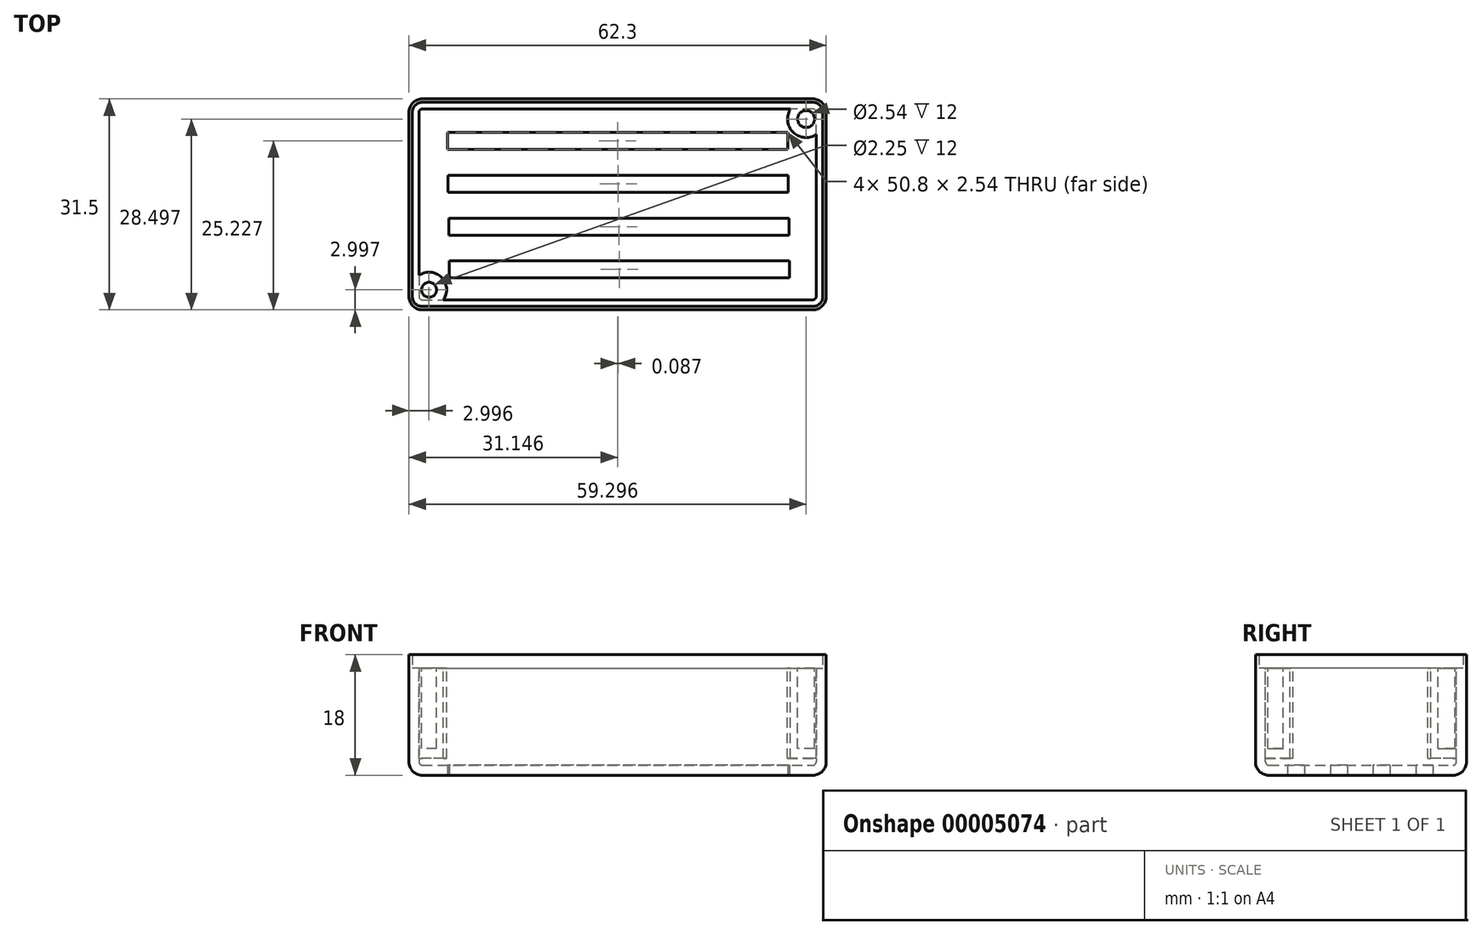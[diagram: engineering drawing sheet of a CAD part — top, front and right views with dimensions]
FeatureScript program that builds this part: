
annotation { "Feature Type Name" : "Feature", "Feature Type Description" : "" }
export const myFeature = defineFeature(function(context is Context, id is Id, definition is map)
    precondition{}
    {
        {
            var Q0;
            Q0=qCreatedBy(makeId("Top.planeOp"),FACE);
            var sketch = newSketch(context, id + "F0", { "sketchPlane" : qUnion([Q0])});
            skLineSegment(sketch, "E0.bottom", {"start": v(-32.94, 23.2) * mm, "end": v(29.36, 23.2) * mm});
            skLineSegment(sketch, "E0.top", {"start": v(-32.94, -8.3) * mm, "end": v(29.36, -8.3) * mm});
            skLineSegment(sketch, "E0.left", {"start": v(-32.94, 23.2) * mm, "end": v(-32.94, -8.3) * mm});
            skLineSegment(sketch, "E0.right", {"start": v(29.36, 23.2) * mm, "end": v(29.36, -8.3) * mm});
            skSolve(sketch);
        }
        {
            var Q0;
            Q0=makeQuery(id+"F0.imprint","IMPRINT",FACE,{"disambiguationData":[TD([[makeQuery(id+"F0.imprint","IMPRINT",EDGE,{"derivedFrom":sQuery(id+"F0.wireOp",EDGE,"E0.bottom")}),-1.0]])]});
            extrude(context, id + "F1", {"entities" : qUnion([Q0]), "depth" : 16 * mm});
        }
        {
            var Q0;
            Q0=makeQuery(id+"F1.opExtrude","CAP_FACE",FACE,{"disambiguationData":[OSD([sQuery(id+"F0.wireOp",EDGE,"E0.bottom"),sQuery(id+"F0.wireOp",EDGE,"E0.top"),sQuery(id+"F0.wireOp",EDGE,"E0.left"),sQuery(id+"F0.wireOp",EDGE,"E0.right")])],"isStart":false});
            var sketch = newSketch(context, id + "F2", { "sketchPlane" : qUnion([Q0])});
            skCircle(sketch, "E1", {"center": v(-29.94, -5.3) * mm, "radius": 1.13 * mm});
            skCircle(sketch, "E2", {"center": v(26.36, 20.2) * mm, "radius": 1.27 * mm});
            skSolve(sketch);
        }
        {
            var Q0;
            Q0=makeQuery(id+"F1.opExtrude","SWEPT_EDGE",EDGE,{"disambiguationData":[OSD([sQuery(id+"F0.wireOp",EDGE,"E0.top"),sQuery(id+"F0.wireOp",EDGE,"E0.left")])]});
            var Q1;
            Q1=makeQuery(id+"F1.opExtrude","SWEPT_EDGE",EDGE,{"disambiguationData":[OSD([sQuery(id+"F0.wireOp",EDGE,"E0.top"),sQuery(id+"F0.wireOp",EDGE,"E0.right")])]});
            var Q2;
            Q2=makeQuery(id+"F1.opExtrude","SWEPT_EDGE",EDGE,{"disambiguationData":[OSD([sQuery(id+"F0.wireOp",EDGE,"E0.bottom"),sQuery(id+"F0.wireOp",EDGE,"E0.right")])]});
            var Q3;
            Q3=makeQuery(id+"F1.opExtrude","SWEPT_EDGE",EDGE,{"disambiguationData":[OSD([sQuery(id+"F0.wireOp",EDGE,"E0.bottom"),sQuery(id+"F0.wireOp",EDGE,"E0.left")])]});
            var Q4;
            Q4=makeQuery(id+"F1.opExtrude","CAP_FACE",FACE,{"disambiguationData":[OSD([sQuery(id+"F0.wireOp",EDGE,"E0.bottom"),sQuery(id+"F0.wireOp",EDGE,"E0.top"),sQuery(id+"F0.wireOp",EDGE,"E0.left"),sQuery(id+"F0.wireOp",EDGE,"E0.right")])],"isStart":true});
            fillet(context, id + "F3", {"entities" : qUnion([Q0, Q1, Q2, Q3, Q4]), "radius" : 2 * mm, "tangentPropagation" : true, "allowEdgeOverflow" : false});
        }
        {
            var Q0;
            Q0=makeQuery(id+"F2.imprint","IMPRINT",FACE,{"disambiguationData":[TD([[makeQuery(id+"F2.imprint","IMPRINT",EDGE,{"derivedFrom":sQuery(id+"F2.wireOp",EDGE,"E1")}),1.0]])]});
            var Q1;
            Q1=makeQuery(id+"F2.imprint","IMPRINT",FACE,{"disambiguationData":[TD([[makeQuery(id+"F2.imprint","IMPRINT",EDGE,{"derivedFrom":sQuery(id+"F2.wireOp",EDGE,"E2")}),1.0]])]});
            var Q2;
            Q2=sQuery(id+"F2.wireOp",EDGE,"E1");
            var Q3;
            Q3=sQuery(id+"F2.wireOp",EDGE,"E2");
            extrude(context, id + "F4", {"entities" : qUnion([Q0, Q1]), "operationType" : NewBodyOperationType.REMOVE, "surfaceEntities" : qUnion([Q2, Q3]), "oppositeDirection" : true, "depth" : 12 * mm});
        }
        {
            var Q0;
            Q0=makeQuery(id+"F1.opExtrude","CAP_FACE",FACE,{"disambiguationData":[OSD([sQuery(id+"F0.wireOp",EDGE,"E0.bottom"),sQuery(id+"F0.wireOp",EDGE,"E0.top"),sQuery(id+"F0.wireOp",EDGE,"E0.left"),sQuery(id+"F0.wireOp",EDGE,"E0.right")])],"isStart":false});
            shell(context, id + "F5", {"entities" : qUnion([Q0]), "thickness" : 1.5 * mm});
        }
        {
            var Q0;
            Q0=makeQuery(id+"F1.opExtrude","CAP_FACE",FACE,{"disambiguationData":[OSD([sQuery(id+"F0.wireOp",EDGE,"E0.bottom"),sQuery(id+"F0.wireOp",EDGE,"E0.top"),sQuery(id+"F0.wireOp",EDGE,"E0.left"),sQuery(id+"F0.wireOp",EDGE,"E0.right")])],"isStart":false});
            var sketch = newSketch(context, id + "F6", { "sketchPlane" : qUnion([Q0])});
            skLineSegment(sketch, "E3.0", {"start": v(-30.94, 22.7) * mm, "end": v(27.36, 22.7) * mm});
            skLineSegment(sketch, "E3.1", {"start": v(-32.44, 21.2) * mm, "end": v(-32.44, -6.3) * mm});
            skLineSegment(sketch, "E3.2", {"start": v(-30.94, -7.8) * mm, "end": v(27.36, -7.8) * mm});
            skLineSegment(sketch, "E3.3", {"start": v(28.86, 21.2) * mm, "end": v(28.86, -6.3) * mm});
            skPoint(sketch, "E4.visualSharp", {"position": v(-32.44, 22.7) * mm});
            skArc(sketch, "E4.filletArc", {"start": v(-30.94, 22.7) * mm, "mid": v(-32, 22.27) * mm, "end": v(-32.44, 21.2) * mm});
            skPoint(sketch, "E5.visualSharp", {"position": v(-32.44, -7.8) * mm});
            skArc(sketch, "E5.filletArc", {"start": v(-32.44, -6.3) * mm, "mid": v(-32, -7.35) * mm, "end": v(-30.94, -7.8) * mm});
            skPoint(sketch, "E6.visualSharp", {"position": v(28.86, 22.7) * mm});
            skArc(sketch, "E6.filletArc", {"start": v(28.86, 21.2) * mm, "mid": v(28.42, 22.27) * mm, "end": v(27.36, 22.7) * mm});
            skPoint(sketch, "E7.visualSharp", {"position": v(28.86, -7.8) * mm});
            skArc(sketch, "E7.filletArc", {"start": v(27.36, -7.8) * mm, "mid": v(28.42, -7.35) * mm, "end": v(28.86, -6.3) * mm});
            skSolve(sketch);
        }
        {
            var Q0;
            Q0=makeQuery(id+"F6.imprint","IMPRINT",FACE,{"disambiguationData":[TD([[makeQuery(id+"F6.imprint","IMPRINT",EDGE,{"derivedFrom":sQuery(id+"F6.wireOp",EDGE,"E3.0")}),1.0]])]});
            extrude(context, id + "F7", {"entities" : qUnion([Q0]), "operationType" : NewBodyOperationType.ADD, "depth" : 2 * mm});
        }
        {
            var Q0;
            Q0=makeQuery(id+"F1.opExtrude","CAP_FACE",FACE,{"disambiguationData":[OSD([sQuery(id+"F0.wireOp",EDGE,"E0.bottom"),sQuery(id+"F0.wireOp",EDGE,"E0.top"),sQuery(id+"F0.wireOp",EDGE,"E0.left"),sQuery(id+"F0.wireOp",EDGE,"E0.right")])],"isStart":true});
            var sketch = newSketch(context, id + "F8", { "sketchPlane" : qUnion([Q0])});
            skLineSegment(sketch, "E8.bottom", {"start": v(23.6, -18.2) * mm, "end": v(-27.2, -18.2) * mm});
            skLineSegment(sketch, "E8.top", {"start": v(23.6, -15.67) * mm, "end": v(-27.2, -15.67) * mm});
            skLineSegment(sketch, "E8.left", {"start": v(23.6, -18.2) * mm, "end": v(23.6, -15.67) * mm});
            skLineSegment(sketch, "E8.right", {"start": v(-27.2, -18.2) * mm, "end": v(-27.2, -15.67) * mm});
            skLineSegment(sketch, "E9", {"start": v(-1.8, -18.2) * mm, "end": v(-1.8, -21.2) * mm});
            skLineSegment(sketch, "E10.1.0.0", {"start": v(-27.1, -11.8) * mm, "end": v(-27.1, -9.27) * mm});
            skLineSegment(sketch, "E10.1.0.1", {"start": v(23.7, -11.8) * mm, "end": v(23.7, -9.27) * mm});
            skLineSegment(sketch, "E10.1.0.2", {"start": v(23.7, -9.27) * mm, "end": v(-27.1, -9.27) * mm});
            skLineSegment(sketch, "E10.1.0.3", {"start": v(23.7, -11.8) * mm, "end": v(-27.1, -11.8) * mm});
            skLineSegment(sketch, "E10.2.0.0", {"start": v(-27.02, -5.4) * mm, "end": v(-27.02, -2.87) * mm});
            skLineSegment(sketch, "E10.2.0.1", {"start": v(23.78, -5.4) * mm, "end": v(23.78, -2.87) * mm});
            skLineSegment(sketch, "E10.2.0.2", {"start": v(23.78, -2.87) * mm, "end": v(-27.02, -2.87) * mm});
            skLineSegment(sketch, "E10.2.0.3", {"start": v(23.78, -5.4) * mm, "end": v(-27.02, -5.4) * mm});
            skLineSegment(sketch, "E10.3.0.0", {"start": v(-26.93, 1) * mm, "end": v(-26.93, 3.53) * mm});
            skLineSegment(sketch, "E10.3.0.1", {"start": v(23.87, 1) * mm, "end": v(23.87, 3.53) * mm});
            skLineSegment(sketch, "E10.3.0.2", {"start": v(23.87, 3.53) * mm, "end": v(-26.93, 3.53) * mm});
            skLineSegment(sketch, "E10.3.0.3", {"start": v(23.87, 1) * mm, "end": v(-26.93, 1) * mm});
            skLineSegment(sketch, "E10.direction1", {"start": v(-27.2, -18.2) * mm, "end": v(-27.1, -11.8) * mm, "construction": true});
            skSolve(sketch);
        }
        {
            var Q0;
            Q0 = qSketchRegion(id + "F8", true);
            extrude(context, id + "F9", {"entities" : qUnion([Q0]), "operationType" : NewBodyOperationType.REMOVE, "endBound" : BoundingType.UP_TO_NEXT, "oppositeDirection" : true, "depth" : 25 * mm});
        }
    });
